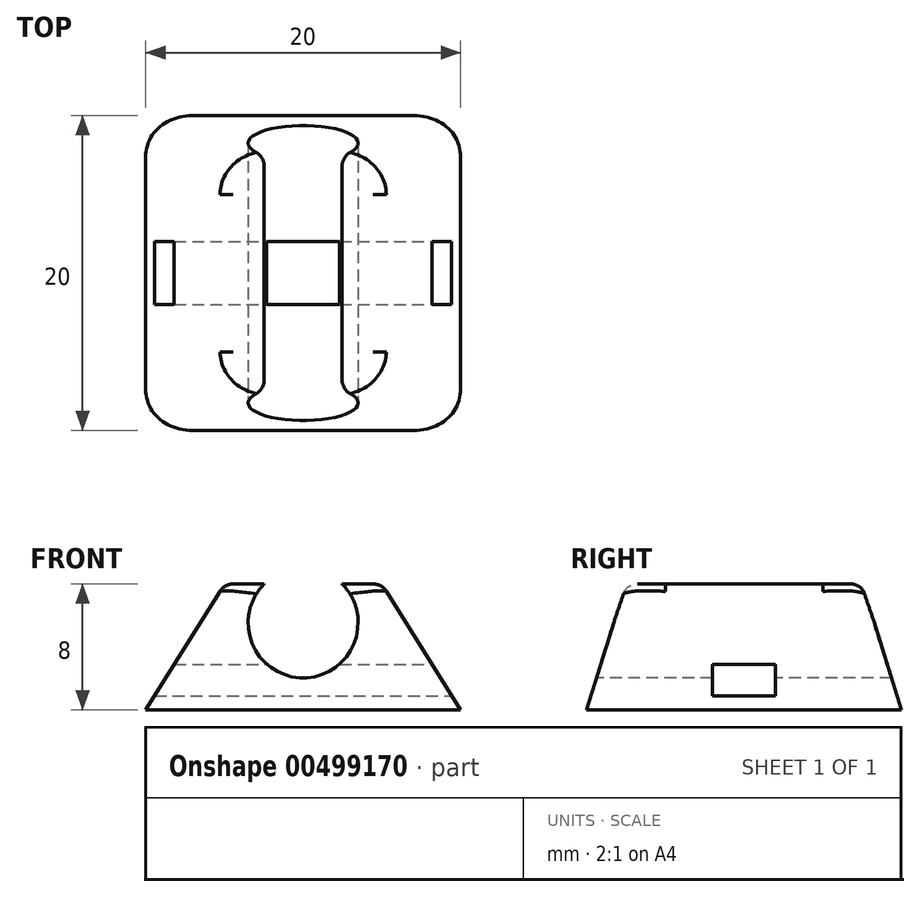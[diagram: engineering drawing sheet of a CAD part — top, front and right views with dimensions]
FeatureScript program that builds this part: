
annotation { "Feature Type Name" : "Feature", "Feature Type Description" : "" }
export const myFeature = defineFeature(function(context is Context, id is Id, definition is map)
    precondition{}
    {
        {
            var Q0;
            Q0=qCreatedBy(makeId("Top.planeOp"),FACE);
            var sketch = newSketch(context, id + "F0", { "sketchPlane" : qUnion([Q0])});
            skLineSegment(sketch, "E0.bottom", {"start": v(10, -10) * mm, "end": v(-10, -10) * mm});
            skLineSegment(sketch, "E0.top", {"start": v(10, 10) * mm, "end": v(-10, 10) * mm});
            skLineSegment(sketch, "E0.left", {"start": v(10, -10) * mm, "end": v(10, 10) * mm});
            skLineSegment(sketch, "E0.right", {"start": v(-10, -10) * mm, "end": v(-10, 10) * mm});
            skPoint(sketch, "E0.middle", {"position": v(0, 0) * mm});
            skSolve(sketch);
        }
        {
            var Q0;
            Q0=makeQuery(id+"F0.imprint","IMPRINT",FACE,{"disambiguationData":[TD([[makeQuery(id+"F0.imprint","IMPRINT",EDGE,{"derivedFrom":sQuery(id+"F0.wireOp",EDGE,"E0.bottom")}),-1.0]])]});
            cPlane(context, id + "F1", {"entities" : qUnion([Q0]), "cplaneType" : CPlaneType.OFFSET, "offset" : 8 * mm, "width" : 150 * mm, "height" : 150 * mm});
        }
        {
            var Q0;
            Q0=qCreatedBy(id+"F1.planeOp",FACE);
            var sketch = newSketch(context, id + "F2", { "sketchPlane" : qUnion([Q0])});
            skLineSegment(sketch, "E1.bottom", {"start": v(5, -7.5) * mm, "end": v(-5, -7.5) * mm});
            skLineSegment(sketch, "E1.top", {"start": v(5, 7.5) * mm, "end": v(-5, 7.5) * mm});
            skLineSegment(sketch, "E1.left", {"start": v(5, -7.5) * mm, "end": v(5, 7.5) * mm});
            skLineSegment(sketch, "E1.right", {"start": v(-5, -7.5) * mm, "end": v(-5, 7.5) * mm});
            skPoint(sketch, "E1.middle", {"position": v(0, 0) * mm});
            skSolve(sketch);
        }
        {
            var Q0;
            Q0=makeQuery(id+"F0.imprint","IMPRINT",FACE,{"disambiguationData":[TD([[makeQuery(id+"F0.imprint","IMPRINT",EDGE,{"derivedFrom":sQuery(id+"F0.wireOp",EDGE,"E0.bottom")}),-1.0]])]});
            var Q1;
            Q1=makeQuery(id+"F2.imprint","IMPRINT",FACE,{"disambiguationData":[TD([[makeQuery(id+"F2.imprint","IMPRINT",EDGE,{"derivedFrom":sQuery(id+"F2.wireOp",EDGE,"E1.bottom")}),-1.0]])]});
            loft(context, id + "F3", {"sheetProfilesArray" : [{ "sheetProfileEntities" : qUnion([Q0]) }, { "sheetProfileEntities" : qUnion([Q1]) }]});
        }
        {
            var Q0;
            Q0=makeQuery(id+"F3.opLoft","SWEPT_EDGE",EDGE,{"disambiguationData":[OSD([sQuery(id+"F0.wireOp",EDGE,"E0.bottom"),sQuery(id+"F0.wireOp",EDGE,"E0.right"),sQuery(id+"F2.wireOp",EDGE,"E1.bottom"),sQuery(id+"F2.wireOp",EDGE,"E1.right")])]});
            var Q1;
            Q1=makeQuery(id+"F3.opLoft","SWEPT_EDGE",EDGE,{"disambiguationData":[OSD([sQuery(id+"F0.wireOp",EDGE,"E0.bottom"),sQuery(id+"F0.wireOp",EDGE,"E0.left"),sQuery(id+"F2.wireOp",EDGE,"E1.bottom"),sQuery(id+"F2.wireOp",EDGE,"E1.left")])]});
            var Q2;
            Q2=makeQuery(id+"F3.opLoft","SWEPT_EDGE",EDGE,{"disambiguationData":[OSD([sQuery(id+"F0.wireOp",EDGE,"E0.top"),sQuery(id+"F0.wireOp",EDGE,"E0.left"),sQuery(id+"F2.wireOp",EDGE,"E1.top"),sQuery(id+"F2.wireOp",EDGE,"E1.left")])]});
            var Q3;
            Q3=makeQuery(id+"F3.opLoft","SWEPT_EDGE",EDGE,{"disambiguationData":[OSD([sQuery(id+"F0.wireOp",EDGE,"E0.top"),sQuery(id+"F0.wireOp",EDGE,"E0.right"),sQuery(id+"F2.wireOp",EDGE,"E1.top"),sQuery(id+"F2.wireOp",EDGE,"E1.right")])]});
            fillet(context, id + "F4", {"entities" : qUnion([Q0, Q1, Q2, Q3]), "radius" : 3 * mm, "tangentPropagation" : true, "allowEdgeOverflow" : false});
        }
        {
            var Q0;
            Q0=qCreatedBy(makeId("Front.planeOp"),FACE);
            var Q1;
            {var subQ0=sQuery(id+"F0.wireOp",EDGE,"E0.bottom");var subQ1=sQuery(id+"F0.wireOp",EDGE,"E0.left");var subQ2=sQuery(id+"F0.wireOp",EDGE,"E0.right");var subQ3=sQuery(id+"F2.wireOp",EDGE,"E1.left");var subQ4=sQuery(id+"F2.wireOp",EDGE,"E1.bottom");Q1=makeQuery(id+"F4.opFillet","BLEND_VERTEX",VERTEX,{"blendedFrom":[makeQuery(id+"F3.opLoft","SWEPT_EDGE",EDGE,{"disambiguationData":[OSD([subQ0,subQ1,subQ4,subQ3])]}),makeQuery(id+"F3.opLoft","SWEPT_FACE",FACE,{"disambiguationData":[OSD([subQ0,subQ1,subQ2,subQ4,subQ3,sQuery(id+"F2.wireOp",EDGE,"E1.right")])]}),makeQuery(id+"F3.opLoft","CAP_FACE",FACE,{"disambiguationData":[OSD([makeQuery(id+"F0.imprint","IMPRINT",FACE,{"disambiguationData":[TD([[makeQuery(id+"F0.imprint","IMPRINT",EDGE,{"derivedFrom":subQ0}),-1.0]])]})])],"isStart":true})],"blendedInto":[makeQuery(id+"F3.opLoft","SWEPT_FACE",FACE,{"disambiguationData":[OSD([subQ0,subQ1,subQ2,subQ4,subQ3,sQuery(id+"F2.wireOp",EDGE,"E1.right")])]}),makeQuery(id+"F3.opLoft","CAP_FACE",FACE,{"disambiguationData":[OSD([makeQuery(id+"F0.imprint","IMPRINT",FACE,{"disambiguationData":[TD([[makeQuery(id+"F0.imprint","IMPRINT",EDGE,{"derivedFrom":subQ0}),-1.0]])]})])],"isStart":true})]});}
            cPlane(context, id + "F5", {"entities" : qUnion([Q0, Q1]), "cplaneType" : CPlaneType.PLANE_POINT, "offset" : 25 * mm, "width" : 150 * mm, "height" : 150 * mm});
        }
        {
            var Q0;
            Q0=qCreatedBy(id+"F5.planeOp",FACE);
            var sketch = newSketch(context, id + "F6", { "sketchPlane" : qUnion([Q0])});
            skCircle(sketch, "E2", {"center": v(0, 5.52) * mm, "radius": 3.5 * mm});
            skSolve(sketch);
        }
        {
            var Q0;
            Q0=makeQuery(id+"F6.imprint","IMPRINT",FACE,{"disambiguationData":[TD([[makeQuery(id+"F6.imprint","IMPRINT",EDGE,{"derivedFrom":sQuery(id+"F6.wireOp",EDGE,"E2")}),1.0]])]});
            var Q1;
            Q1=sQuery(id+"F6.wireOp",EDGE,"E2");
            extrude(context, id + "F7", {"entities" : qUnion([Q0]), "operationType" : NewBodyOperationType.REMOVE, "surfaceEntities" : qUnion([Q1]), "oppositeDirection" : true, "depth" : 25 * mm, "offsetDistance" : 25 * mm});
        }
        {
            var Q0;
            Q0=qCreatedBy(makeId("Right.planeOp"),FACE);
            var Q1;
            {var subQ0=sQuery(id+"F0.wireOp",EDGE,"E0.bottom");var subQ1=sQuery(id+"F0.wireOp",EDGE,"E0.top");var subQ2=sQuery(id+"F0.wireOp",EDGE,"E0.left");var subQ3=sQuery(id+"F2.wireOp",EDGE,"E1.left");var subQ4=sQuery(id+"F2.wireOp",EDGE,"E1.top");Q1=makeQuery(id+"F4.opFillet","BLEND_VERTEX",VERTEX,{"blendedFrom":[makeQuery(id+"F3.opLoft","SWEPT_EDGE",EDGE,{"disambiguationData":[OSD([subQ1,subQ2,subQ4,subQ3])]}),makeQuery(id+"F3.opLoft","SWEPT_FACE",FACE,{"disambiguationData":[OSD([subQ0,subQ1,subQ2,sQuery(id+"F2.wireOp",EDGE,"E1.bottom"),subQ4,subQ3])]}),makeQuery(id+"F3.opLoft","CAP_FACE",FACE,{"disambiguationData":[OSD([makeQuery(id+"F0.imprint","IMPRINT",FACE,{"disambiguationData":[TD([[makeQuery(id+"F0.imprint","IMPRINT",EDGE,{"derivedFrom":subQ0}),-1.0]])]})])],"isStart":true})],"blendedInto":[makeQuery(id+"F3.opLoft","SWEPT_FACE",FACE,{"disambiguationData":[OSD([subQ0,subQ1,subQ2,sQuery(id+"F2.wireOp",EDGE,"E1.bottom"),subQ4,subQ3])]}),makeQuery(id+"F3.opLoft","CAP_FACE",FACE,{"disambiguationData":[OSD([makeQuery(id+"F0.imprint","IMPRINT",FACE,{"disambiguationData":[TD([[makeQuery(id+"F0.imprint","IMPRINT",EDGE,{"derivedFrom":subQ0}),-1.0]])]})])],"isStart":true})]});}
            cPlane(context, id + "F8", {"entities" : qUnion([Q0, Q1]), "cplaneType" : CPlaneType.PLANE_POINT, "offset" : 25 * mm, "width" : 150 * mm, "height" : 150 * mm});
        }
        {
            var Q0;
            Q0=qCreatedBy(id+"F8.planeOp",FACE);
            var sketch = newSketch(context, id + "F9", { "sketchPlane" : qUnion([Q0])});
            skLineSegment(sketch, "E3.bottom", {"start": v(2, 2.9) * mm, "end": v(-2, 2.9) * mm});
            skLineSegment(sketch, "E3.top", {"start": v(2, 0.9) * mm, "end": v(-2, 0.9) * mm});
            skLineSegment(sketch, "E3.left", {"start": v(2, 2.9) * mm, "end": v(2, 0.9) * mm});
            skLineSegment(sketch, "E3.right", {"start": v(-2, 2.9) * mm, "end": v(-2, 0.9) * mm});
            skPoint(sketch, "E3.middle", {"position": v(0, 1.9) * mm});
            skSolve(sketch);
        }
        {
            var Q0;
            Q0=makeQuery(id+"F9.imprint","IMPRINT",FACE,{"disambiguationData":[TD([[makeQuery(id+"F9.imprint","IMPRINT",EDGE,{"derivedFrom":sQuery(id+"F9.wireOp",EDGE,"E3.bottom")}),1.0]])]});
            extrude(context, id + "F10", {"entities" : qUnion([Q0]), "operationType" : NewBodyOperationType.REMOVE, "oppositeDirection" : true, "depth" : 25 * mm, "offsetDistance" : 25 * mm});
        }
        {
            var Q0;
            Q0=makeQuery(id+"F3.opLoft","MID_CAP_EDGE",EDGE,{"disambiguationData":[OSD([sQuery(id+"F2.wireOp",EDGE,"E1.bottom"),sQuery(id+"F2.wireOp",EDGE,"E1.top"),sQuery(id+"F2.wireOp",EDGE,"E1.left")])],"capPos":1.0});
            var Q1;
            Q1=makeQuery(id+"F3.opLoft","MID_CAP_EDGE",EDGE,{"disambiguationData":[OSD([sQuery(id+"F2.wireOp",EDGE,"E1.bottom"),sQuery(id+"F2.wireOp",EDGE,"E1.top"),sQuery(id+"F2.wireOp",EDGE,"E1.right")])],"capPos":1.0});
            fillet(context, id + "F11", {"entities" : qUnion([Q0, Q1]), "radius" : 1 * mm, "tangentPropagation" : true, "allowEdgeOverflow" : false});
        }
    });
